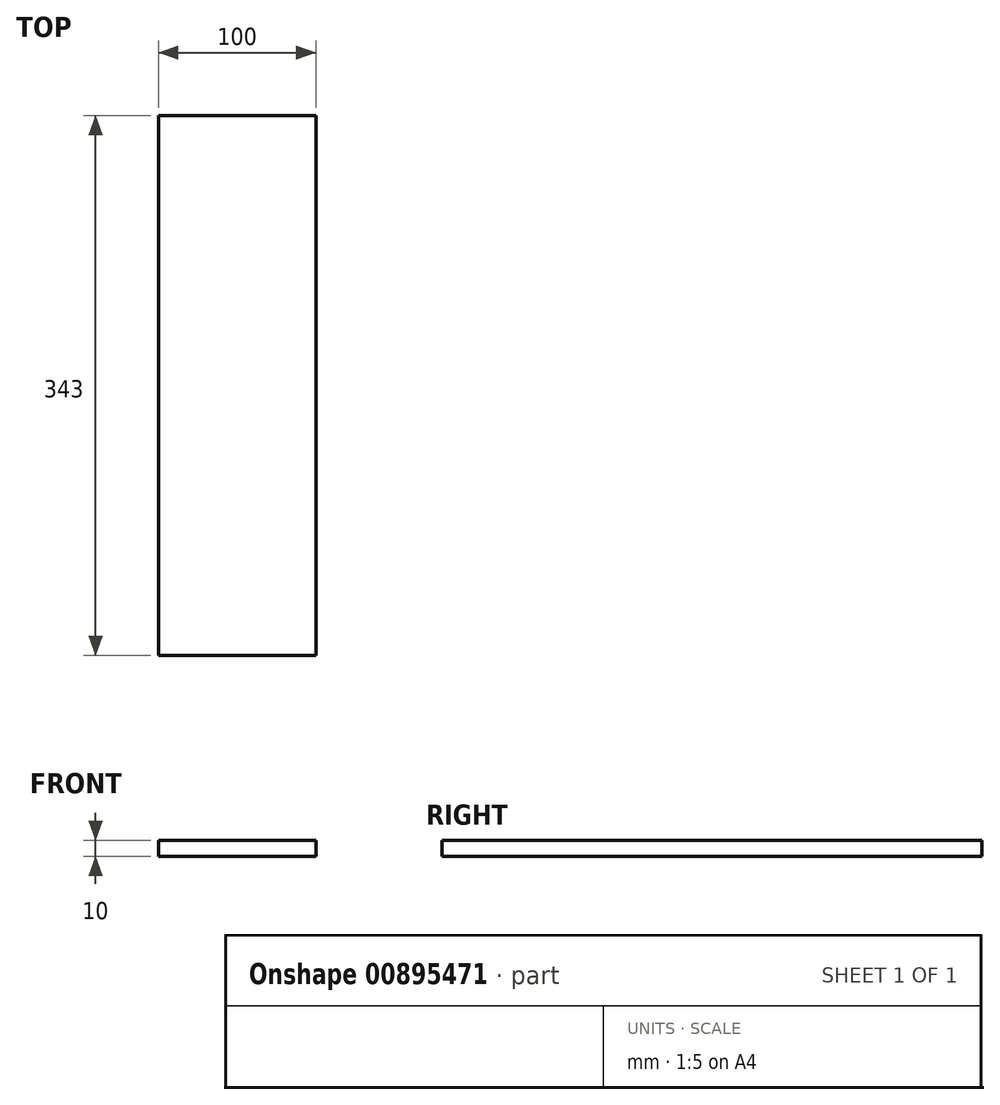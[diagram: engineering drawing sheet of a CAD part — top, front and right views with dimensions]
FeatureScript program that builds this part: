
annotation { "Feature Type Name" : "Feature", "Feature Type Description" : "" }
export const myFeature = defineFeature(function(context is Context, id is Id, definition is map)
    precondition{}
    {
        {
            var Q0;
            Q0=qCreatedBy(makeId("Top.planeOp"),FACE);
            var sketch = newSketch(context, id + "F0", { "sketchPlane" : qUnion([Q0])});
            skLineSegment(sketch, "E0.bottom", {"start": v(50, 171.5) * mm, "end": v(-50, 171.5) * mm});
            skLineSegment(sketch, "E0.top", {"start": v(50, -171.5) * mm, "end": v(-50, -171.5) * mm});
            skLineSegment(sketch, "E0.left", {"start": v(50, 171.5) * mm, "end": v(50, -171.5) * mm});
            skLineSegment(sketch, "E0.right", {"start": v(-50, 171.5) * mm, "end": v(-50, -171.5) * mm});
            skPoint(sketch, "E0.middle", {"position": v(0, 0) * mm});
            skSolve(sketch);
        }
        {
            var Q0;
            Q0 = qSketchRegion(id + "F0", true);
            extrude(context, id + "F1", {"entities" : qUnion([Q0]), "depth" : 10 * mm, "offsetDistance" : 25 * mm});
        }
    });
